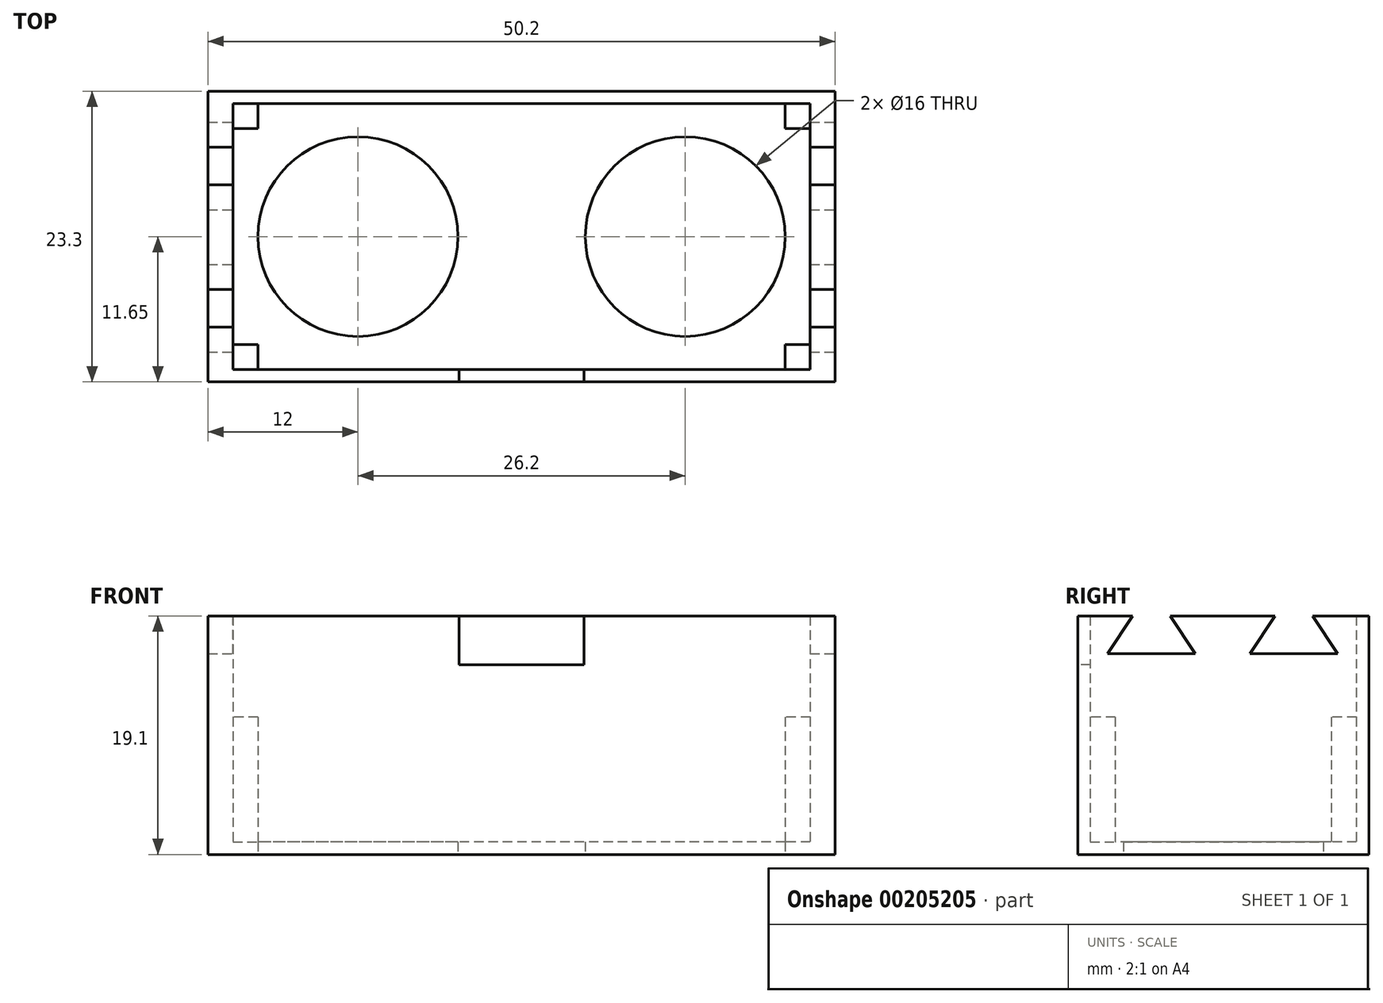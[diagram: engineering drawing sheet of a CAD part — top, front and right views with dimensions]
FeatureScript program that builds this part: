
annotation { "Feature Type Name" : "Feature", "Feature Type Description" : "" }
export const myFeature = defineFeature(function(context is Context, id is Id, definition is map)
    precondition{}
    {
        {
            var Q0;
            Q0=qCreatedBy(makeId("Top.planeOp"),FACE);
            var sketch = newSketch(context, id + "F0", { "sketchPlane" : qUnion([Q0])});
            skLineSegment(sketch, "E0", {"start": v(-22.55, 10.1) * mm, "end": v(22.55, 10.1) * mm, "construction": true});
            skLineSegment(sketch, "E1", {"start": v(22.55, 10.1) * mm, "end": v(22.55, -10.1) * mm, "construction": true});
            skLineSegment(sketch, "E2", {"start": v(22.55, -10.1) * mm, "end": v(-22.55, -10.1) * mm, "construction": true});
            skLineSegment(sketch, "E3", {"start": v(-22.55, -10.1) * mm, "end": v(-22.55, 10.1) * mm, "construction": true});
            skLineSegment(sketch, "E4", {"start": v(-22.55, 10.1) * mm, "end": v(-20.4, 10.1) * mm, "construction": true});
            skLineSegment(sketch, "E5", {"start": v(22.55, 10.1) * mm, "end": v(20.9, 10.1) * mm, "construction": true});
            skLineSegment(sketch, "E6", {"start": v(-20.4, 10.1) * mm, "end": v(-20.4, -10.1) * mm, "construction": true});
            skLineSegment(sketch, "E7", {"start": v(21.35, 0) * mm, "end": v(-20.4, 0) * mm, "construction": true});
            skLineSegment(sketch, "E8", {"start": v(-20.4, 0) * mm, "end": v(-13.1, 0) * mm, "construction": true});
            skLineSegment(sketch, "E9", {"start": v(21.35, 0) * mm, "end": v(13.1, 0) * mm, "construction": true});
            skCircle(sketch, "E10", {"center": v(-13.1, 0) * mm, "radius": 8 * mm});
            skCircle(sketch, "E11", {"center": v(13.1, 0) * mm, "radius": 8 * mm});
            skLineSegment(sketch, "E12", {"start": v(-5.1, 0) * mm, "end": v(5.1, 0) * mm});
            skLineSegment(sketch, "E13.0", {"start": v(-23.1, 10.65) * mm, "end": v(23.1, 10.65) * mm});
            skLineSegment(sketch, "E13.1", {"start": v(-23.1, -10.65) * mm, "end": v(-23.1, 10.65) * mm});
            skLineSegment(sketch, "E13.2", {"start": v(23.1, -10.65) * mm, "end": v(-23.1, -10.65) * mm});
            skLineSegment(sketch, "E13.3", {"start": v(23.1, 10.65) * mm, "end": v(23.1, -10.65) * mm});
            skLineSegment(sketch, "E14.0", {"start": v(-24.1, 11.65) * mm, "end": v(24.1, 11.65) * mm});
            skLineSegment(sketch, "E14.2", {"start": v(24.4, -11.65) * mm, "end": v(-24.1, -11.65) * mm});
            skLineSegment(sketch, "E15", {"start": v(-5.25, 10.1) * mm, "end": v(-5.25, 9.1) * mm, "construction": true});
            skLineSegment(sketch, "E16", {"start": v(-3, 9.1) * mm, "end": v(3.68, 9.1) * mm, "construction": true});
            skLineSegment(sketch, "E17", {"start": v(0, 0) * mm, "end": v(0, 9.1) * mm, "construction": true});
            skLineSegment(sketch, "E18", {"start": v(-3, 5.1) * mm, "end": v(3.68, 5.1) * mm, "construction": true});
            skArc(sketch, "E19", {"start": v(-3, 9.1) * mm, "mid": v(-5, 7.1) * mm, "end": v(-3, 5.1) * mm, "construction": true});
            skArc(sketch, "E20", {"start": v(3.68, 5.1) * mm, "mid": v(5.68, 7.1) * mm, "end": v(3.68, 9.1) * mm, "construction": true});
            skLineSegment(sketch, "E21", {"start": v(24.1, 11.65) * mm, "end": v(25.1, 11.65) * mm});
            skLineSegment(sketch, "E22", {"start": v(25.1, 11.65) * mm, "end": v(25.1, -11.65) * mm});
            skLineSegment(sketch, "E23", {"start": v(25.1, -11.65) * mm, "end": v(24.4, -11.65) * mm});
            skLineSegment(sketch, "E24.MirrorCS", {"start": v(-25.1, 11.65) * mm, "end": v(-25.1, -11.65) * mm});
            skLineSegment(sketch, "E25.MirrorCS", {"start": v(-24.1, 11.65) * mm, "end": v(-25.1, 11.65) * mm});
            skLineSegment(sketch, "E26", {"start": v(-24.1, -11.65) * mm, "end": v(-25.1, -11.65) * mm});
            skSolve(sketch);
        }
        {
            var Q0;
            Q0=makeQuery(id+"F0.imprint","IMPRINT",FACE,{"disambiguationData":[TD([[makeQuery(id+"F0.imprint","IMPRINT",EDGE,{"derivedFrom":sQuery(id+"F0.wireOp",EDGE,"E13.0")}),1.0]])]});
            extrude(context, id + "F1", {"entities" : qUnion([Q0]), "depth" : 19.1 * mm});
        }
        {
            var Q0;
            Q0=makeQuery(id+"F0.imprint","IMPRINT",FACE,{"disambiguationData":[TD([[makeQuery(id+"F0.imprint","IMPRINT",EDGE,{"derivedFrom":sQuery(id+"F0.wireOp",EDGE,"E13.0")}),-1.0]])]});
            extrude(context, id + "F2", {"entities" : qUnion([Q0]), "operationType" : NewBodyOperationType.ADD, "depth" : 1 * mm});
        }
        {
            var Q0;
            Q0=makeQuery(id+"F1.opExtrude","SWEPT_FACE",FACE,{"disambiguationData":[OSD([sQuery(id+"F0.wireOp",EDGE,"E14.2")])]});
            var sketch = newSketch(context, id + "F3", { "sketchPlane" : qUnion([Q0])});
            skLineSegment(sketch, "E27", {"start": v(24.65, 0) * mm, "end": v(21.1, 0) * mm, "construction": true});
            skLineSegment(sketch, "E28", {"start": v(21.1, 0) * mm, "end": v(21.1, -0.8) * mm, "construction": true});
            skLineSegment(sketch, "E29", {"start": v(21.1, -0.8) * mm, "end": v(5.1, -0.8) * mm, "construction": true});
            skLineSegment(sketch, "E30", {"start": v(5.1, -0.8) * mm, "end": v(5.1, 0) * mm, "construction": true});
            skLineSegment(sketch, "E31", {"start": v(-24.05, 0.02) * mm, "end": v(-21.1, 0) * mm, "construction": true});
            skLineSegment(sketch, "E32", {"start": v(-21.1, 0) * mm, "end": v(-21.1, -0.8) * mm, "construction": true});
            skLineSegment(sketch, "E33", {"start": v(-21.1, -0.8) * mm, "end": v(-5.1, -0.8) * mm, "construction": true});
            skLineSegment(sketch, "E34", {"start": v(-5.1, -0.8) * mm, "end": v(-5.1, 0) * mm, "construction": true});
            skLineSegment(sketch, "E35", {"start": v(-5, 17.2) * mm, "end": v(5, 17.2) * mm, "construction": true});
            skLineSegment(sketch, "E36", {"start": v(-5.1, 0) * mm, "end": v(5.1, 0) * mm, "construction": true});
            skLineSegment(sketch, "E37", {"start": v(0, 0) * mm, "end": v(0, 17.2) * mm, "construction": true});
            skLineSegment(sketch, "E38", {"start": v(-5, 17.2) * mm, "end": v(-5, 19.2) * mm, "construction": true});
            skLineSegment(sketch, "E39", {"start": v(-5, 17.2) * mm, "end": v(-5, 15.2) * mm, "construction": true});
            skLineSegment(sketch, "E40", {"start": v(-5, 15.2) * mm, "end": v(5, 15.2) * mm});
            skLineSegment(sketch, "E41", {"start": v(-5, 19.2) * mm, "end": v(5, 19.2) * mm});
            skLineSegment(sketch, "E42", {"start": v(5, 19.2) * mm, "end": v(5, 15.2) * mm});
            skLineSegment(sketch, "E43", {"start": v(-5, 19.2) * mm, "end": v(-5, 15.2) * mm});
            skSolve(sketch);
        }
        {
            var Q0;
            {var subQ0=sQuery(id+"F3.wireOp",EDGE,"E41");Q0=makeQuery(id+"F3.imprint","IMPRINT",FACE,{"disambiguationData":[TD([[makeQuery(id+"F3.imprint","IMPRINT",EDGE,{"derivedFrom":subQ0}),-1.0]])]});}
            var Q1;
            {var subQ0=sQuery(id+"F3.wireOp",EDGE,"E40");Q1=makeQuery(id+"F3.imprint","IMPRINT",FACE,{"disambiguationData":[TD([[makeQuery(id+"F3.imprint","IMPRINT",EDGE,{"derivedFrom":subQ0}),1.0]])]});}
            extrude(context, id + "F4", {"entities" : qUnion([Q0, Q1]), "operationType" : NewBodyOperationType.REMOVE, "oppositeDirection" : true, "depth" : 4 * mm});
        }
        {
            var Q0;
            Q0=qCreatedBy(makeId("Right.planeOp"),FACE);
            var sketch = newSketch(context, id + "F5", { "sketchPlane" : qUnion([Q0])});
            skLineSegment(sketch, "E44", {"start": v(-11.7, 19.1) * mm, "end": v(11.6, 19.1) * mm, "construction": true});
            skLineSegment(sketch, "E45", {"start": v(-0.05, 18) * mm, "end": v(5.65, 18) * mm, "construction": true});
            skLineSegment(sketch, "E46", {"start": v(5.65, 18) * mm, "end": v(7.15, 19.1) * mm, "construction": true});
            skLineSegment(sketch, "E47", {"start": v(5.65, 18) * mm, "end": v(5.65, 15) * mm, "construction": true});
            skLineSegment(sketch, "E48", {"start": v(7.15, 19.1) * mm, "end": v(9.15, 16.1) * mm});
            skLineSegment(sketch, "E49", {"start": v(-0.05, 18) * mm, "end": v(-0.05, -2.74) * mm, "construction": true});
            skLineSegment(sketch, "E50.MirrorCS", {"start": v(-4.25, 19.1) * mm, "end": v(-2.25, 16.1) * mm});
            skLineSegment(sketch, "E51.MirrorCS", {"start": v(-7.25, 19.1) * mm, "end": v(-9.25, 16.1) * mm});
            skLineSegment(sketch, "E52", {"start": v(-9.25, 16.1) * mm, "end": v(-2.25, 16.1) * mm});
            skLineSegment(sketch, "E53", {"start": v(-7.25, 19.1) * mm, "end": v(-4.25, 19.1) * mm});
            skPoint(sketch, "E54", {"position": v(-5.75, 19.1) * mm});
            skLineSegment(sketch, "E55.MirrorCS", {"start": v(4.15, 19.1) * mm, "end": v(2.15, 16.1) * mm});
            skLineSegment(sketch, "E56.MirrorCS", {"start": v(11.6, 19.1) * mm, "end": v(-11.7, 19.1) * mm, "construction": true});
            skLineSegment(sketch, "E57", {"start": v(4.15, 19.1) * mm, "end": v(7.15, 19.1) * mm});
            skLineSegment(sketch, "E58", {"start": v(9.15, 16.1) * mm, "end": v(2.15, 16.1) * mm});
            skSolve(sketch);
        }
        {
            var Q0;
            Q0=makeQuery(id+"F5.imprint","IMPRINT",FACE,{"disambiguationData":[TD([[makeQuery(id+"F5.imprint","IMPRINT",EDGE,{"derivedFrom":sQuery(id+"F5.wireOp",EDGE,"E55.MirrorCS")}),1.0]])]});
            var Q1;
            Q1=makeQuery(id+"F5.imprint","IMPRINT",FACE,{"disambiguationData":[TD([[makeQuery(id+"F5.imprint","IMPRINT",EDGE,{"derivedFrom":sQuery(id+"F5.wireOp",EDGE,"E50.MirrorCS")}),-1.0]])]});
            extrude(context, id + "F6", {"entities" : qUnion([Q0, Q1]), "operationType" : NewBodyOperationType.REMOVE, "oppositeDirection" : true, "depth" : 56 * mm, "symmetric" : true});
        }
        {
            var Q0;
            Q0=makeQuery(id+"F2.opExtrude","CAP_FACE",FACE,{"disambiguationData":[OSD([sQuery(id+"F0.wireOp",EDGE,"E10"),sQuery(id+"F0.wireOp",EDGE,"E11"),sQuery(id+"F0.wireOp",EDGE,"E13.0"),sQuery(id+"F0.wireOp",EDGE,"E13.1"),sQuery(id+"F0.wireOp",EDGE,"E13.2"),sQuery(id+"F0.wireOp",EDGE,"E13.3")])],"isStart":false});
            var sketch = newSketch(context, id + "F7", { "sketchPlane" : qUnion([Q0])});
            skLineSegment(sketch, "E59.bottom", {"start": v(-23.1, 10.65) * mm, "end": v(-21.1, 10.65) * mm});
            skLineSegment(sketch, "E59.top", {"start": v(-23.1, 8.65) * mm, "end": v(-21.1, 8.65) * mm});
            skLineSegment(sketch, "E59.left", {"start": v(-23.1, 10.65) * mm, "end": v(-23.1, 8.65) * mm});
            skLineSegment(sketch, "E59.right", {"start": v(-21.1, 10.65) * mm, "end": v(-21.1, 8.65) * mm});
            skLineSegment(sketch, "E60.bottom", {"start": v(23.1, 10.65) * mm, "end": v(21.1, 10.65) * mm});
            skLineSegment(sketch, "E60.top", {"start": v(23.1, 8.65) * mm, "end": v(21.1, 8.65) * mm});
            skLineSegment(sketch, "E60.left", {"start": v(23.1, 10.65) * mm, "end": v(23.1, 8.65) * mm});
            skLineSegment(sketch, "E60.right", {"start": v(21.1, 10.65) * mm, "end": v(21.1, 8.65) * mm});
            skLineSegment(sketch, "E61.bottom", {"start": v(-23.1, -10.65) * mm, "end": v(-21.1, -10.65) * mm});
            skLineSegment(sketch, "E61.top", {"start": v(-23.1, -8.65) * mm, "end": v(-21.1, -8.65) * mm});
            skLineSegment(sketch, "E61.left", {"start": v(-23.1, -10.65) * mm, "end": v(-23.1, -8.65) * mm});
            skLineSegment(sketch, "E61.right", {"start": v(-21.1, -10.65) * mm, "end": v(-21.1, -8.65) * mm});
            skLineSegment(sketch, "E62.bottom", {"start": v(23.1, -10.65) * mm, "end": v(21.1, -10.65) * mm});
            skLineSegment(sketch, "E62.top", {"start": v(23.1, -8.65) * mm, "end": v(21.1, -8.65) * mm});
            skLineSegment(sketch, "E62.left", {"start": v(23.1, -10.65) * mm, "end": v(23.1, -8.65) * mm});
            skLineSegment(sketch, "E62.right", {"start": v(21.1, -10.65) * mm, "end": v(21.1, -8.65) * mm});
            skSolve(sketch);
        }
        {
            var Q0;
            Q0=makeQuery(id+"F7.imprint","IMPRINT",FACE,{"disambiguationData":[TD([[makeQuery(id+"F7.imprint","IMPRINT",EDGE,{"derivedFrom":sQuery(id+"F7.wireOp",EDGE,"E59.bottom")}),-1.0]])]});
            var Q1;
            Q1=makeQuery(id+"F7.imprint","IMPRINT",FACE,{"disambiguationData":[TD([[makeQuery(id+"F7.imprint","IMPRINT",EDGE,{"derivedFrom":sQuery(id+"F7.wireOp",EDGE,"E61.bottom")}),-1.0]])]});
            var Q2;
            Q2=makeQuery(id+"F7.imprint","IMPRINT",FACE,{"disambiguationData":[TD([[makeQuery(id+"F7.imprint","IMPRINT",EDGE,{"derivedFrom":sQuery(id+"F7.wireOp",EDGE,"E62.bottom")}),-1.0]])]});
            var Q3;
            Q3=makeQuery(id+"F7.imprint","IMPRINT",FACE,{"disambiguationData":[TD([[makeQuery(id+"F7.imprint","IMPRINT",EDGE,{"derivedFrom":sQuery(id+"F7.wireOp",EDGE,"E60.bottom")}),-1.0]])]});
            extrude(context, id + "F8", {"entities" : qUnion([Q0, Q1, Q2, Q3]), "operationType" : NewBodyOperationType.ADD, "depth" : 10 * mm});
        }
    });
